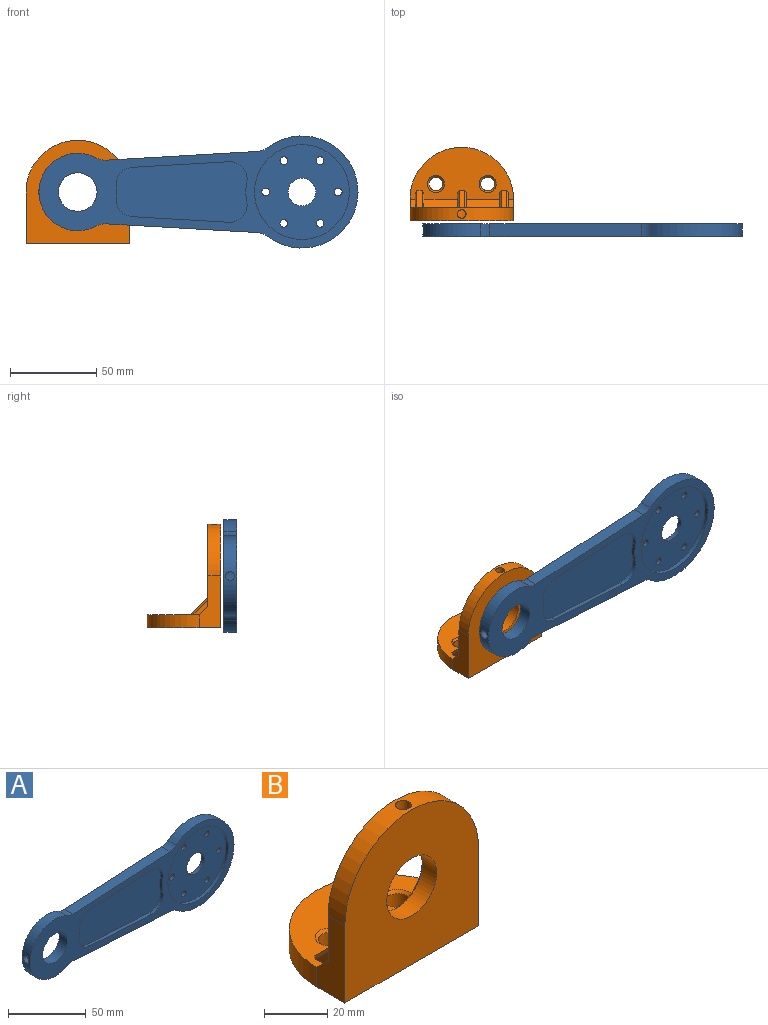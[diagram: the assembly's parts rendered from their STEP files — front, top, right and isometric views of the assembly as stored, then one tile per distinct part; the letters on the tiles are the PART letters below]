
ASSEMBLY  parts=2 mates=1
PART A: 41 faces, bbox 185x7.5x65 mm
  f0: plane 55x55mm, normal (0,-1,0), area 2079.3mm2, adj f2,f3,f4,f5,f6,f7,f8,f36
  f1: plane 55x55mm, normal (0,1,0), area 2079.3mm2, adj f2,f3,f4,f5,f6,f7,f8,f9
  f2: cylinder r=2.25mm len=4.5mm, axis (0,1,0), area 35.3mm2, adj f0,f1
  f3: cylinder r=2.25mm len=4.5mm, axis (0,1,0), area 35.3mm2, adj f0,f1
  f4: cylinder r=2.25mm len=4.5mm, axis (0,1,0), area 35.3mm2, adj f0,f1
  f5: cylinder r=8mm len=16mm, axis (0,1,0), area 125.7mm2, adj f0,f1
  f6: cylinder r=2.25mm len=4.5mm, axis (0,1,0), area 35.3mm2, adj f0,f1
  f7: cylinder r=2.25mm len=4.5mm, axis (0,1,0), area 35.3mm2, adj f0,f1
  f8: cylinder r=2.25mm len=4.5mm, axis (0,1,0), area 35.3mm2, adj f0,f1
  f9: cylinder r=27.5mm len=55mm, axis (0,1,0), area 432mm2, adj f1,f18
  f10: cylinder r=22.5mm len=6mm, axis (0,1,0), area 15mm2, adj f11,f17,f18,f28
  f11: cylinder r=10mm len=11.32mm, axis (0,1,0), area 41.2mm2, adj f10,f12,f18,f28
  f12: plane 55.97x3.23mm, normal (0.06,0,1), area 140.2mm2, adj f11,f13,f18,f28
  f13: cylinder r=10mm len=11.78mm, axis (0,1,0), area 45.2mm2, adj f12,f14,f18,f28
  f14: cylinder r=32.5mm len=11.57mm, axis (0,1,0), area 29.1mm2, adj f13,f15,f18,f28
  f15: cylinder r=10mm len=11.78mm, axis (0,1,0), area 45.2mm2, adj f14,f16,f18,f28
  f16: plane 55.97x3.23mm, normal (0.06,0,-1), area 140.2mm2, adj f15,f17,f18,f28
  f17: cylinder r=10mm len=11.32mm, axis (0,1,0), area 41.2mm2, adj f10,f16,f18,f28
  f18: plane 185x65mm, normal (0,1,0), area 3207.4mm2, adj f9,f10,f11,f12,f13,f14,f15,f16
  f19: cylinder r=11.2mm len=22.4mm, axis (0,1,0), area 506.4mm2, adj f18,f38,f40
  f20: plane 88.1x7.5mm, normal (-0.06,0,1), area 661.9mm2, adj f18,f21,f22,f38
  f21: cylinder r=10mm len=7.5mm, axis (0,1,0), area 45.4mm2, adj f18,f20,f27,f38
  f22: cylinder r=10mm len=7.5mm, axis (0,1,0), area 42.3mm2, adj f18,f20,f26,f38
  f23: cylinder r=10mm len=7.5mm, axis (0,1,0), area 45.4mm2, adj f18,f24,f27,f38
  f24: plane 88.1x7.5mm, normal (-0.06,0,-1), area 661.9mm2, adj f18,f23,f25,f38
  f25: cylinder r=10mm len=7.5mm, axis (0,1,0), area 42.3mm2, adj f18,f24,f26,f38
  f26: cylinder r=22.5mm len=45mm, axis (0,1,0), area 679.7mm2, adj f18,f22,f25,f38,f40
  f27: cylinder r=32.5mm len=65mm, axis (0,1,0), area 1088.8mm2, adj f18,f21,f23,f38
  f28: plane 75.97x35.12mm, normal (0,1,0), area 2331.6mm2, adj f10,f11,f12,f13,f14,f15,f16,f17
  f29: cylinder r=10mm len=11.32mm, axis (0,1,0), area 41.2mm2, adj f30,f37,f38,f39
  f30: plane 55.97x3.23mm, normal (0.06,0,-1), area 140.2mm2, adj f29,f31,f38,f39
  f31: cylinder r=10mm len=11.78mm, axis (0,1,0), area 45.2mm2, adj f30,f32,f38,f39
  f32: cylinder r=32.5mm len=11.57mm, axis (0,1,0), area 29.1mm2, adj f31,f33,f38,f39
  f33: cylinder r=10mm len=11.78mm, axis (0,1,0), area 45.2mm2, adj f32,f34,f38,f39
  f34: plane 55.97x3.23mm, normal (0.06,0,1), area 140.2mm2, adj f33,f35,f38,f39
  f35: cylinder r=10mm len=11.32mm, axis (0,1,0), area 41.2mm2, adj f34,f37,f38,f39
  f36: cylinder r=27.5mm len=55mm, axis (0,1,0), area 432mm2, adj f0,f38
  f37: cylinder r=22.5mm len=6mm, axis (0,1,0), area 15mm2, adj f29,f35,f38,f39
  f38: plane 185x65mm, normal (0,-1,0), area 3207.4mm2, adj f19,f20,f21,f22,f23,f24,f25,f26
  f39: plane 75.97x35.12mm, normal (0,-1,0), area 2331.6mm2, adj f29,f30,f31,f32,f33,f34,f35,f37
  f40: cylinder r=2.6mm len=11.61mm, axis (1,0,0), area 185.9mm2, adj f19,f26
PART B: 36 faces, bbox 60x42.5x60 mm
  f0: cylinder r=11.2mm len=22.4mm, axis (0,-1,0), area 437.7mm2, adj f4,f15,f35
  f1: cylinder r=30mm len=60mm, axis (0,1,0), area 687.2mm2, adj f3,f4,f6,f7,f35
  f2: plane 60x30mm, normal (0,0,1), area 1185.9mm2, adj f10,f13,f14,f16,f17,f18,f19,f20
  f3: plane 60x47.5mm, normal (0,1,0), area 1925.4mm2, adj f1,f6,f7,f15,f16,f17,f18,f19
  f4: plane 60x60mm, normal (0,-1,0), area 2819.6mm2, adj f0,f1,f5,f6,f7
  f5: plane 60x42.5mm, normal (0,0,-1), area 2006.6mm2, adj f4,f6,f7,f10,f11,f12
  f6: plane 30x12.5mm, normal (1,0,0), area 275mm2, adj f1,f3,f4,f5,f10,f31
  f7: plane 30x12.5mm, normal (-1,0,0), area 275mm2, adj f1,f3,f4,f5,f10,f32
  f8: cylinder r=4mm len=8mm, axis (0,0,1), area 138.2mm2, adj f12,f14
  f9: cylinder r=4mm len=8mm, axis (0,0,1), area 138.2mm2, adj f11,f13
  f10: cylinder r=30mm len=60mm, axis (0,0,-1), area 706.9mm2, adj f2,f5,f6,f7
  f11: cone r=5mm half-angle=45deg, axis (0,0,-1), area 40mm2, adj f5,f9
  f12: cone r=5mm half-angle=45deg, axis (0,0,-1), area 40mm2, adj f5,f8
  f13: cone r=4mm half-angle=45deg, axis (0,0,1), area 40mm2, adj f2,f9
  f14: cone r=4mm half-angle=45deg, axis (0,0,1), area 40mm2, adj f2,f8
  f15: cone r=11.2mm half-angle=45deg, axis (0,1,0), area 104mm2, adj f0,f3
  f16: plane 10x10mm, normal (0,0.71,0.71), area 42.4mm2, adj f2,f3,f27,f28
  f17: plane 8.59x8.59mm, normal (1,0,0), area 24.4mm2, adj f2,f3,f28,f34
  f18: plane 8.59x8.59mm, normal (-1,0,0), area 24.4mm2, adj f2,f3,f27,f33
  f19: plane 10x10mm, normal (0,0.71,0.71), area 42.4mm2, adj f2,f3,f29,f30
  f20: plane 8.59x8.59mm, normal (1,0,0), area 24.4mm2, adj f2,f3,f30,f31
  f21: plane 8.59x8.59mm, normal (-1,0,0), area 24.4mm2, adj f2,f3,f29,f34
  f22: plane 10x10mm, normal (0,0.71,0.71), area 42.4mm2, adj f2,f3,f25,f26
  f23: plane 8.59x8.59mm, normal (1,0,0), area 24.4mm2, adj f2,f3,f26,f33
  f24: plane 8.59x8.59mm, normal (-1,0,0), area 24.4mm2, adj f2,f3,f25,f32
  f25: plane 10x10mm, normal (-0.71,0.5,0.5), area 18.6mm2, adj f2,f3,f22,f24
  f26: plane 10x10mm, normal (0.71,0.5,0.5), area 18.6mm2, adj f2,f3,f22,f23
  f27: plane 10x10mm, normal (-0.71,0.5,0.5), area 18.6mm2, adj f2,f3,f16,f18
  f28: plane 10x10mm, normal (0.71,0.5,0.5), area 18.6mm2, adj f2,f3,f16,f17
  f29: plane 10x10mm, normal (-0.71,0.5,0.5), area 18.6mm2, adj f2,f3,f19,f21
  f30: plane 10x10mm, normal (0.71,0.5,0.5), area 18.6mm2, adj f2,f3,f19,f20
  f31: plane 5x5mm, normal (0,0.71,0.71), area 21.2mm2, adj f2,f3,f6,f20
  f32: plane 5x5mm, normal (0,0.71,0.71), area 21.2mm2, adj f2,f3,f7,f24
  f33: plane 19.5x5mm, normal (0,0.71,0.71), area 137.9mm2, adj f2,f3,f18,f23
  f34: plane 19.5x5mm, normal (0,0.71,0.71), area 137.9mm2, adj f2,f3,f17,f21
  f35: cylinder r=2.5mm len=19.08mm, axis (0,0,-1), area 296.7mm2, adj f0,f1
PLACE A rot(axis=(0,1,0),0deg) t=(66,-23.95,30)mm
PLACE B t=(0,-18.45,30)mm
MATE revolute B.f0 <-> A.f19  axis (0,1,0) through (0,-11.95,30)mm
